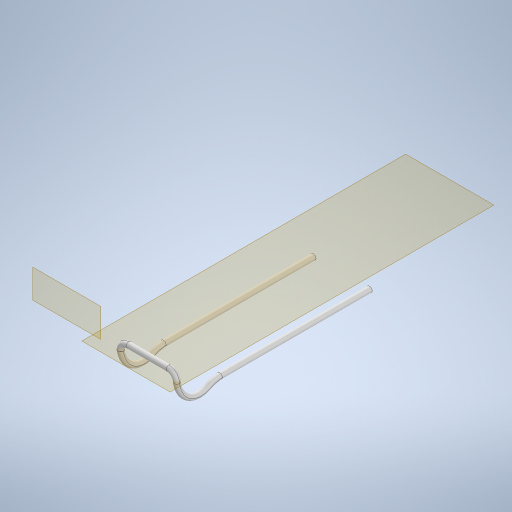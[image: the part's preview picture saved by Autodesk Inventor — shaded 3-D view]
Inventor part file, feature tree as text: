
AUTODESK INVENTOR PART (.ipt)
format: ipt  version: 2024.1 (Build 281209000, 209)  size: 378,368 bytes
history: native  units: mm
features: sketch x5, plane x3, sweep x2, projected_geometry x2, extrude x1, other x1
ambient origin geometry x8: Origin, YZ Plane, XZ Plane, XY Plane, X Axis, Y Axis, Z Axis, Center Point
bodies: Solid1 (feature_tree)
feature tree (14):
  extrude  "Extrusion1"  Depth=105.0mm
  sweep  "Sweep1"
  plane  "Work Plane1"
  plane  "Work Plane3"
  sweep  "Sweep2"
  plane  "Work Plane2"
  sketch  "Sketch2"  dims[d0=10.3mm d1=105.0mm]
  sketch  "Sketch3"  dims[d2=52.5mm d3=280.0mm d4=0.0mm]
  sketch  "Sketch4"  dims[d5=80.0mm d7=0.0mm d8=0.0mm]
  projected_geometry  "Projected Loop1"
  projected_geometry  "Projected Loop2"
  sketch  "Sketch5"  dims[d12=0.0mm d13=0.0mm]
  sketch  "Sketch6"  dims[d15=30.0mm d17=12.0mm d20=15.0mm]
  other  "Work Point2"
